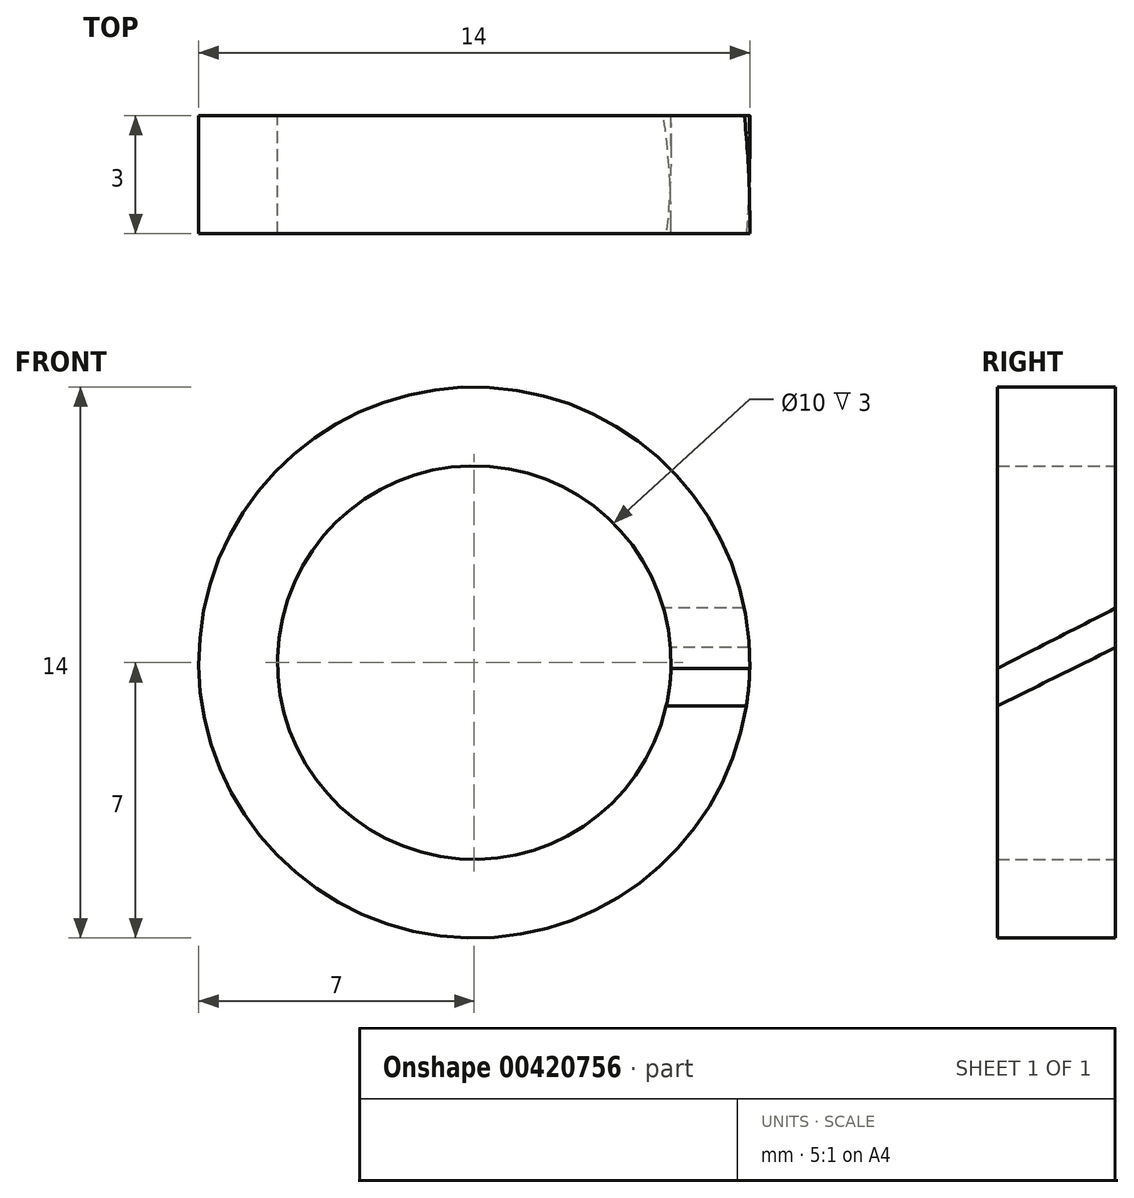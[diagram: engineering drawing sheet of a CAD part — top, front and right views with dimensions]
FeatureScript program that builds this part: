
annotation { "Feature Type Name" : "Feature", "Feature Type Description" : "" }
export const myFeature = defineFeature(function(context is Context, id is Id, definition is map)
    precondition{}
    {
        {
            var Q0;
            Q0=qCreatedBy(makeId("Front.planeOp"),FACE);
            var sketch = newSketch(context, id + "F0", { "sketchPlane" : qUnion([Q0])});
            skCircle(sketch, "E0", {"center": v(0, 0) * mm, "radius": 7 * mm});
            skCircle(sketch, "E1", {"center": v(0, 0) * mm, "radius": 5 * mm});
            skSolve(sketch);
        }
        {
            var Q0;
            Q0 = qSketchRegion(id + "F0", true);
            extrude(context, id + "F1", {"entities" : qUnion([Q0]), "depth" : 3 * mm});
        }
        {
            var Q0;
            Q0=qCreatedBy(makeId("Right.planeOp"),FACE);
            var sketch = newSketch(context, id + "F2", { "sketchPlane" : qUnion([Q0])});
            skLineSegment(sketch, "E2", {"start": v(-4.45, -0.89) * mm, "end": v(0, 1.38) * mm});
            skLineSegment(sketch, "E3", {"start": v(0, 1.38) * mm, "end": v(0, 0.38) * mm});
            skLineSegment(sketch, "E4", {"start": v(0, 0.38) * mm, "end": v(-4.45, -1.82) * mm});
            skLineSegment(sketch, "E5", {"start": v(-4.45, -1.82) * mm, "end": v(-4.45, -0.89) * mm});
            skSolve(sketch);
        }
        {
            var Q0;
            Q0 = qSketchRegion(id + "F2", true);
            extrude(context, id + "F3", {"entities" : qUnion([Q0]), "operationType" : NewBodyOperationType.REMOVE, "depth" : 25 * mm});
        }
    });
